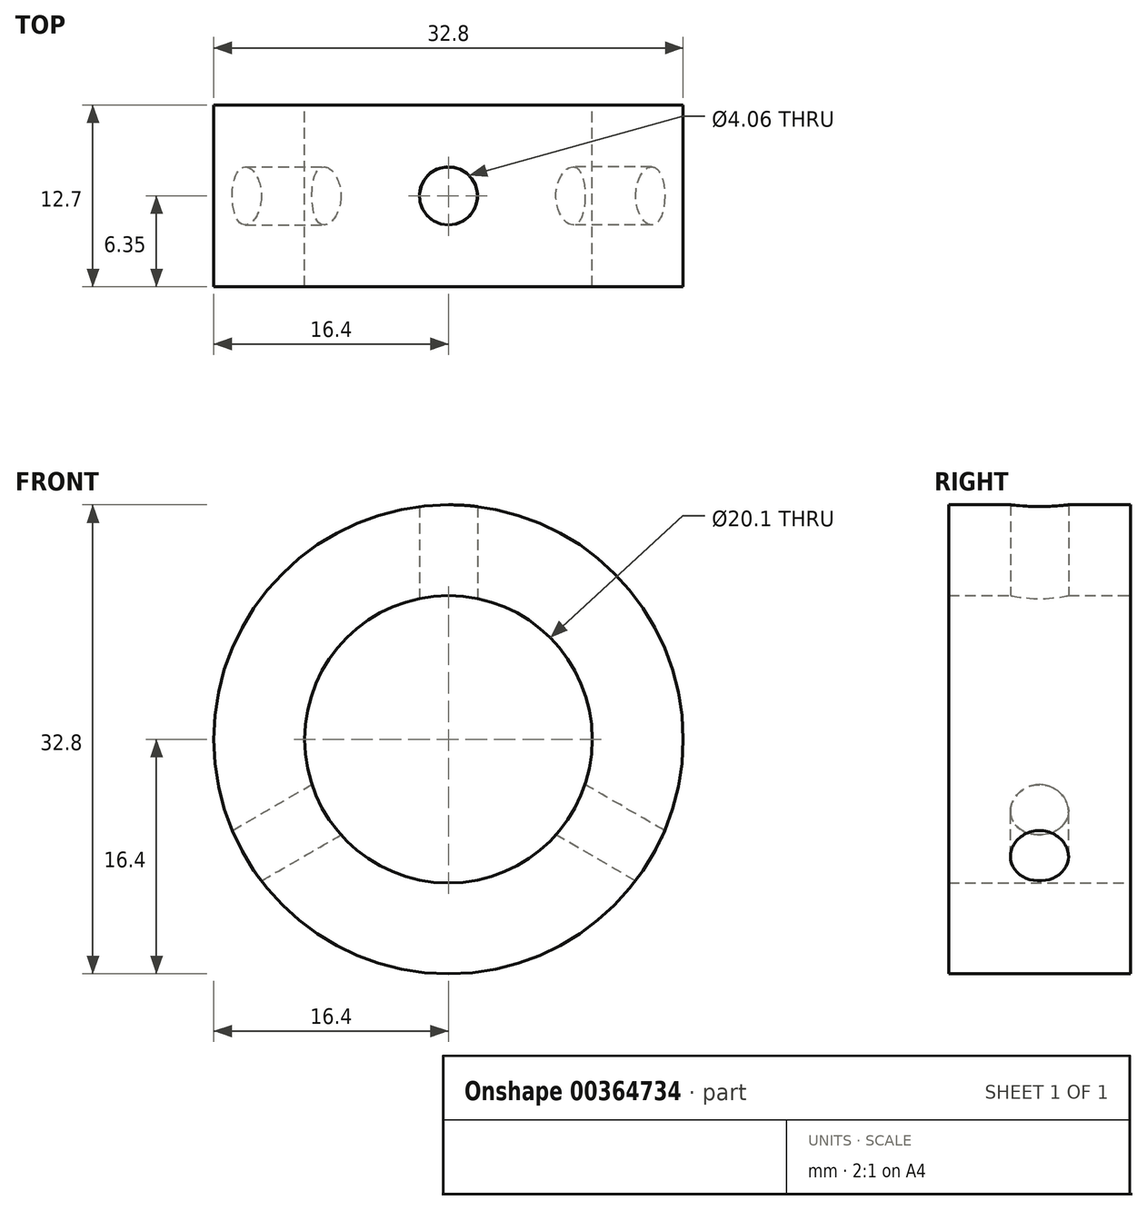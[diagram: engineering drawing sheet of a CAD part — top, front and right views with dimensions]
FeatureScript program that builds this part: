
annotation { "Feature Type Name" : "Feature", "Feature Type Description" : "" }
export const myFeature = defineFeature(function(context is Context, id is Id, definition is map)
    precondition{}
    {
        {
            var Q0;
            Q0=qCreatedBy(makeId("Front.planeOp"),FACE);
            var sketch = newSketch(context, id + "F0", { "sketchPlane" : qUnion([Q0])});
            skCircle(sketch, "E0", {"center": v(0, 0) * mm, "radius": 10.05 * mm});
            skCircle(sketch, "E1", {"center": v(0, 0) * mm, "radius": 16.4 * mm});
            skSolve(sketch);
        }
        {
            var Q0;
            Q0 = qSketchRegion(id + "F0", true);
            extrude(context, id + "F1", {"entities" : qUnion([Q0]), "depth" : 12.7 * mm});
        }
        {
            var Q0;
            Q0=qCreatedBy(makeId("Top.planeOp"),FACE);
            var sketch = newSketch(context, id + "F2", { "sketchPlane" : qUnion([Q0])});
            skCircle(sketch, "E2", {"center": v(0, -6.35) * mm, "radius": 2.03 * mm});
            skSolve(sketch);
        }
        {
            var Q0;
            Q0=makeQuery(id+"F2.imprint","IMPRINT",FACE,{"disambiguationData":[TD([[makeQuery(id+"F2.imprint","IMPRINT",EDGE,{"derivedFrom":sQuery(id+"F2.wireOp",EDGE,"E2")}),1.0]])]});
            extrude(context, id + "F3", {"entities" : qUnion([Q0]), "depth" : 25.4 * mm, "offsetDistance" : 25.4 * mm});
        }
        {
            var Q0;
            Q0=makeQuery(id+"F3.opExtrude","SWEPT_BODY",BODY,{"disambiguationData":[OSD([sQuery(id+"F2.wireOp",EDGE,"E2")])]});
            var Q1;
            Q1=makeQuery(id+"F1.opExtrude","SWEPT_FACE",FACE,{"disambiguationData":[OSD([sQuery(id+"F0.wireOp",EDGE,"E0")])]});
            var Q2;
            Q2=makeQuery(id+"F3.opExtrude","SWEPT_BODY",BODY,{"disambiguationData":[OSD([sQuery(id+"F2.wireOp",EDGE,"E2")])]});
            circularPattern(context, id + "F4", {"operationType" : NewBodyOperationType.REMOVE, "entities" : qUnion([Q0]), "axis" : qUnion([Q1]), "angle" : 360 * degree, "instanceCount" : 3, "equalSpace" : true});
        }
    });
